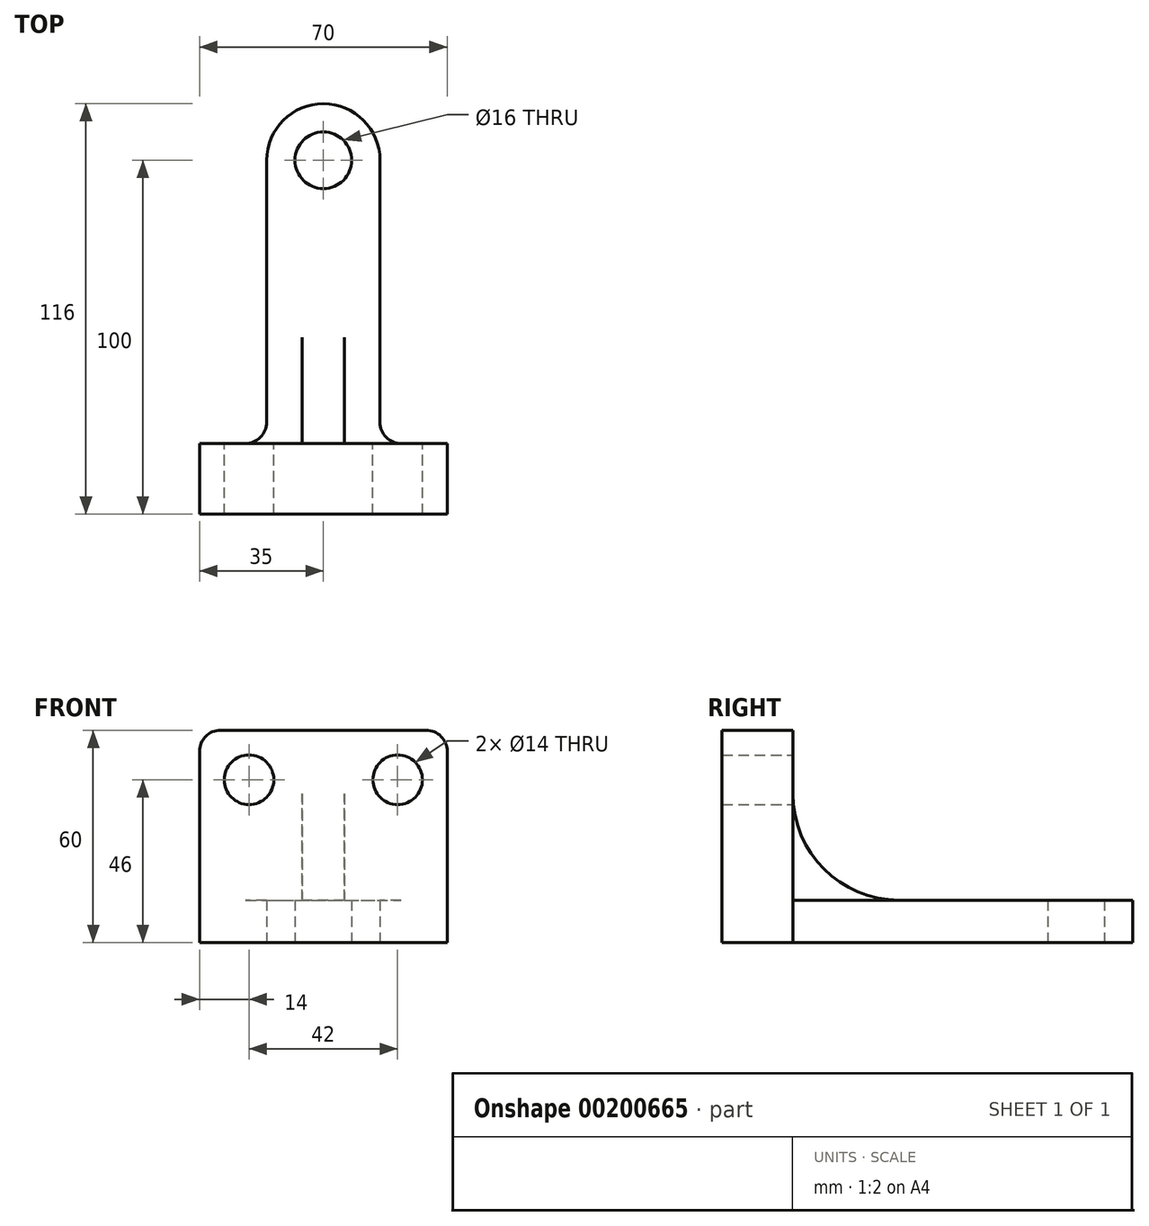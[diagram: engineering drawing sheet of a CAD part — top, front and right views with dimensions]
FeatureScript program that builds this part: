
annotation { "Feature Type Name" : "Feature", "Feature Type Description" : "" }
export const myFeature = defineFeature(function(context is Context, id is Id, definition is map)
    precondition{}
    {
        {
            var Q0;
            Q0=qCreatedBy(makeId("Front.planeOp"),FACE);
            var sketch = newSketch(context, id + "F0", { "sketchPlane" : qUnion([Q0])});
            skLineSegment(sketch, "E0", {"start": v(-35, 0) * mm, "end": v(35, 0) * mm});
            skLineSegment(sketch, "E1", {"start": v(-35, 0) * mm, "end": v(-35, 54) * mm});
            skLineSegment(sketch, "E2", {"start": v(-29, 60) * mm, "end": v(29, 60) * mm});
            skLineSegment(sketch, "E3", {"start": v(35, 54) * mm, "end": v(35, 0) * mm});
            skPoint(sketch, "E4.visualSharp", {"position": v(-35, 60) * mm});
            skArc(sketch, "E4.filletArc", {"start": v(-29, 60) * mm, "mid": v(-33.24, 58.24) * mm, "end": v(-35, 54) * mm});
            skPoint(sketch, "E5.visualSharp", {"position": v(35, 60) * mm});
            skArc(sketch, "E5.filletArc", {"start": v(35, 54) * mm, "mid": v(33.24, 58.24) * mm, "end": v(29, 60) * mm});
            skCircle(sketch, "E6", {"center": v(-21, 46) * mm, "radius": 7 * mm});
            skCircle(sketch, "E7", {"center": v(21, 46) * mm, "radius": 7 * mm});
            skSolve(sketch);
        }
        {
            var Q0;
            Q0 = qSketchRegion(id + "F0", true);
            var Q1;
            Q1=makeQuery(id+"F0.imprint","IMPRINT",FACE,{"disambiguationData":[TD([[makeQuery(id+"F0.imprint","IMPRINT",EDGE,{"derivedFrom":sQuery(id+"F0.wireOp",EDGE,"E0")}),1.0]])]});
            extrude(context, id + "F1", {"entities" : qUnion([Q0, Q1]), "depth" : 20 * mm});
        }
        {
            var Q0;
            Q0=makeQuery(id+"F1.opExtrude","SWEPT_FACE",FACE,{"disambiguationData":[OSD([sQuery(id+"F0.wireOp",EDGE,"E0")])]});
            var sketch = newSketch(context, id + "F2", { "sketchPlane" : qUnion([Q0])});
            skLineSegment(sketch, "E8.0.0", {"start": v(-35, 0) * mm, "end": v(-22, 0) * mm});
            skLineSegment(sketch, "E8.0.1", {"start": v(35, 0) * mm, "end": v(35, 20) * mm});
            skLineSegment(sketch, "E8.0.2", {"start": v(35, 20) * mm, "end": v(-35, 20) * mm});
            skLineSegment(sketch, "E8.0.3", {"start": v(-35, 20) * mm, "end": v(-35, 0) * mm});
            skLineSegment(sketch, "E9", {"start": v(16, -6) * mm, "end": v(16, -80) * mm});
            skLineSegment(sketch, "E10", {"start": v(16, -80) * mm, "end": v(16, -80) * mm});
            skLineSegment(sketch, "E11", {"start": v(-16, -80) * mm, "end": v(-16, -6) * mm});
            skArc(sketch, "E12", {"start": v(-16, -80) * mm, "mid": v(0, -96) * mm, "end": v(16, -80) * mm});
            skLineSegment(sketch, "E13.trimOffspring", {"start": v(-16, -80) * mm, "end": v(-16, -80) * mm});
            skCircle(sketch, "E14", {"center": v(0, -80) * mm, "radius": 8 * mm});
            skLineSegment(sketch, "E15.trimOffspring", {"start": v(22, 0) * mm, "end": v(35, 0) * mm});
            skPoint(sketch, "E16.visualSharp", {"position": v(-16, 0) * mm});
            skArc(sketch, "E16.filletArc", {"start": v(-16, -6) * mm, "mid": v(-17.76, -1.76) * mm, "end": v(-22, 0) * mm});
            skPoint(sketch, "E17.visualSharp", {"position": v(16, 0) * mm});
            skArc(sketch, "E17.filletArc", {"start": v(22, 0) * mm, "mid": v(17.76, -1.76) * mm, "end": v(16, -6) * mm});
            skSolve(sketch);
        }
        {
            var Q0;
            Q0=makeQuery(id+"F2.imprint","IMPRINT",FACE,{"disambiguationData":[TD([[makeQuery(id+"F2.imprint","IMPRINT",EDGE,{"derivedFrom":sQuery(id+"F2.wireOp",EDGE,"E9")}),-1.0]])]});
            extrude(context, id + "F3", {"entities" : qUnion([Q0]), "operationType" : NewBodyOperationType.ADD, "oppositeDirection" : true, "depth" : 12 * mm});
        }
        {
            var Q0;
            Q0=qCreatedBy(makeId("Right.planeOp"),FACE);
            var sketch = newSketch(context, id + "F4", { "sketchPlane" : qUnion([Q0])});
            skLineSegment(sketch, "E18", {"start": v(44.86, -95.9) * mm, "end": v(8.83, -95.9) * mm});
            skLineSegment(sketch, "E19", {"start": v(8.83, -95.9) * mm, "end": v(8.83, -76.34) * mm});
            skLineSegment(sketch, "E20", {"start": v(8.83, -76.34) * mm, "end": v(8.83, -49.03) * mm});
            skLineSegment(sketch, "E21", {"start": v(8.83, -49.03) * mm, "end": v(8.83, -23.48) * mm});
            skLineSegment(sketch, "E22", {"start": v(8.83, -23.48) * mm, "end": v(44.86, -23.48) * mm});
            skLineSegment(sketch, "E23", {"start": v(44.86, -23.48) * mm, "end": v(44.86, -95.9) * mm});
            skSolve(sketch);
        }
        {
            var Q0;
            Q0 = qSketchRegion(id + "F4", true);
            extrude(context, id + "F5", {"entities" : qUnion([Q0]), "depth" : 25 * mm});
        }
        {
            var Q0;
            Q0=makeQuery(id+"F5.opExtrude","SWEPT_BODY",BODY,{"disambiguationData":[OSD([sQuery(id+"F4.wireOp",EDGE,"E18"),sQuery(id+"F4.wireOp",EDGE,"E19"),sQuery(id+"F4.wireOp",EDGE,"E20"),sQuery(id+"F4.wireOp",EDGE,"E21"),sQuery(id+"F4.wireOp",EDGE,"E22"),sQuery(id+"F4.wireOp",EDGE,"E23")])]});
            deleteBodies(context, id + "F6", {"entities" : qUnion([Q0])});
        }
        {
            var Q0;
            Q0=qCreatedBy(makeId("Right.planeOp"),FACE);
            var sketch = newSketch(context, id + "F7", { "sketchPlane" : qUnion([Q0])});
            skLineSegment(sketch, "E24.0", {"start": v(80, 12) * mm, "end": v(0, 12) * mm});
            skLineSegment(sketch, "E25.0", {"start": v(0, 0) * mm, "end": v(0, 54) * mm});
            skPoint(sketch, "E26.orphan", {"position": v(6, 12) * mm});
            skArc(sketch, "E27", {"start": v(0, 42) * mm, "mid": v(8.79, 20.79) * mm, "end": v(30, 12) * mm});
            skSolve(sketch);
        }
        {
            var Q0;
            Q0 = qSketchRegion(id + "F7", true);
            extrude(context, id + "F8", {"entities" : qUnion([Q0]), "operationType" : NewBodyOperationType.ADD, "endBound" : BoundingType.SYMMETRIC, "depth" : 12 * mm});
        }
    });
